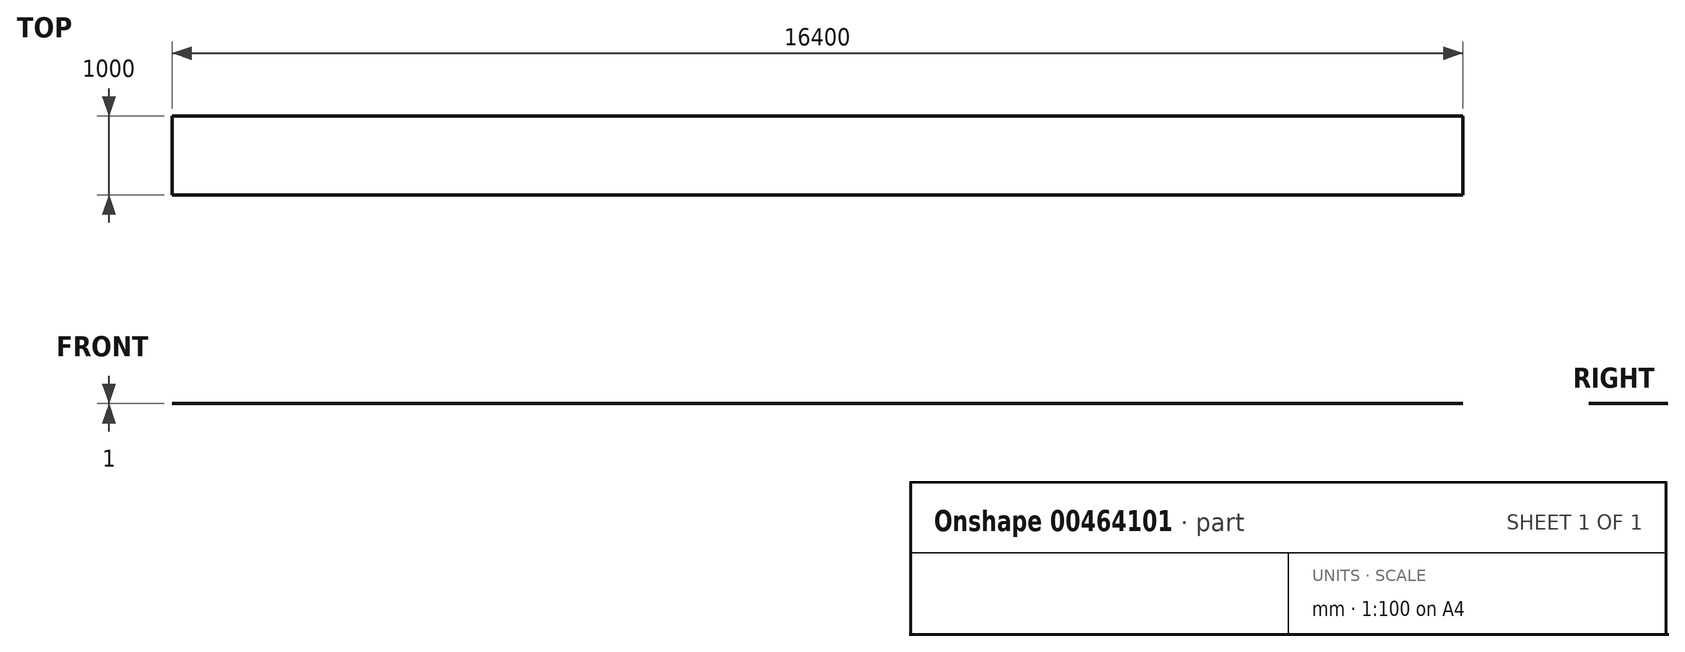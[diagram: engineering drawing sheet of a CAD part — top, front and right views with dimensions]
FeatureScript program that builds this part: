
annotation { "Feature Type Name" : "Feature", "Feature Type Description" : "" }
export const myFeature = defineFeature(function(context is Context, id is Id, definition is map)
    precondition{}
    {
        {
            var Q0;
            Q0=qCreatedBy(makeId("Top.planeOp"),FACE);
            var sketch = newSketch(context, id + "F0", { "sketchPlane" : qUnion([Q0])});
            skLineSegment(sketch, "E0.bottom", {"start": v(0, 0) * mm, "end": v(-16400, 0) * mm});
            skLineSegment(sketch, "E0.top", {"start": v(0, -1000) * mm, "end": v(-16400, -1000) * mm});
            skLineSegment(sketch, "E0.left", {"start": v(0, 0) * mm, "end": v(0, -1000) * mm});
            skLineSegment(sketch, "E0.right", {"start": v(-16400, 0) * mm, "end": v(-16400, -1000) * mm});
            skSolve(sketch);
        }
        {
            var Q0;
            Q0=qSketchRegion(id+"F0",true);
            extrude(context, id + "F1", {"entities" : qUnion([Q0]), "depth" : 1 * mm});
        }
    });
